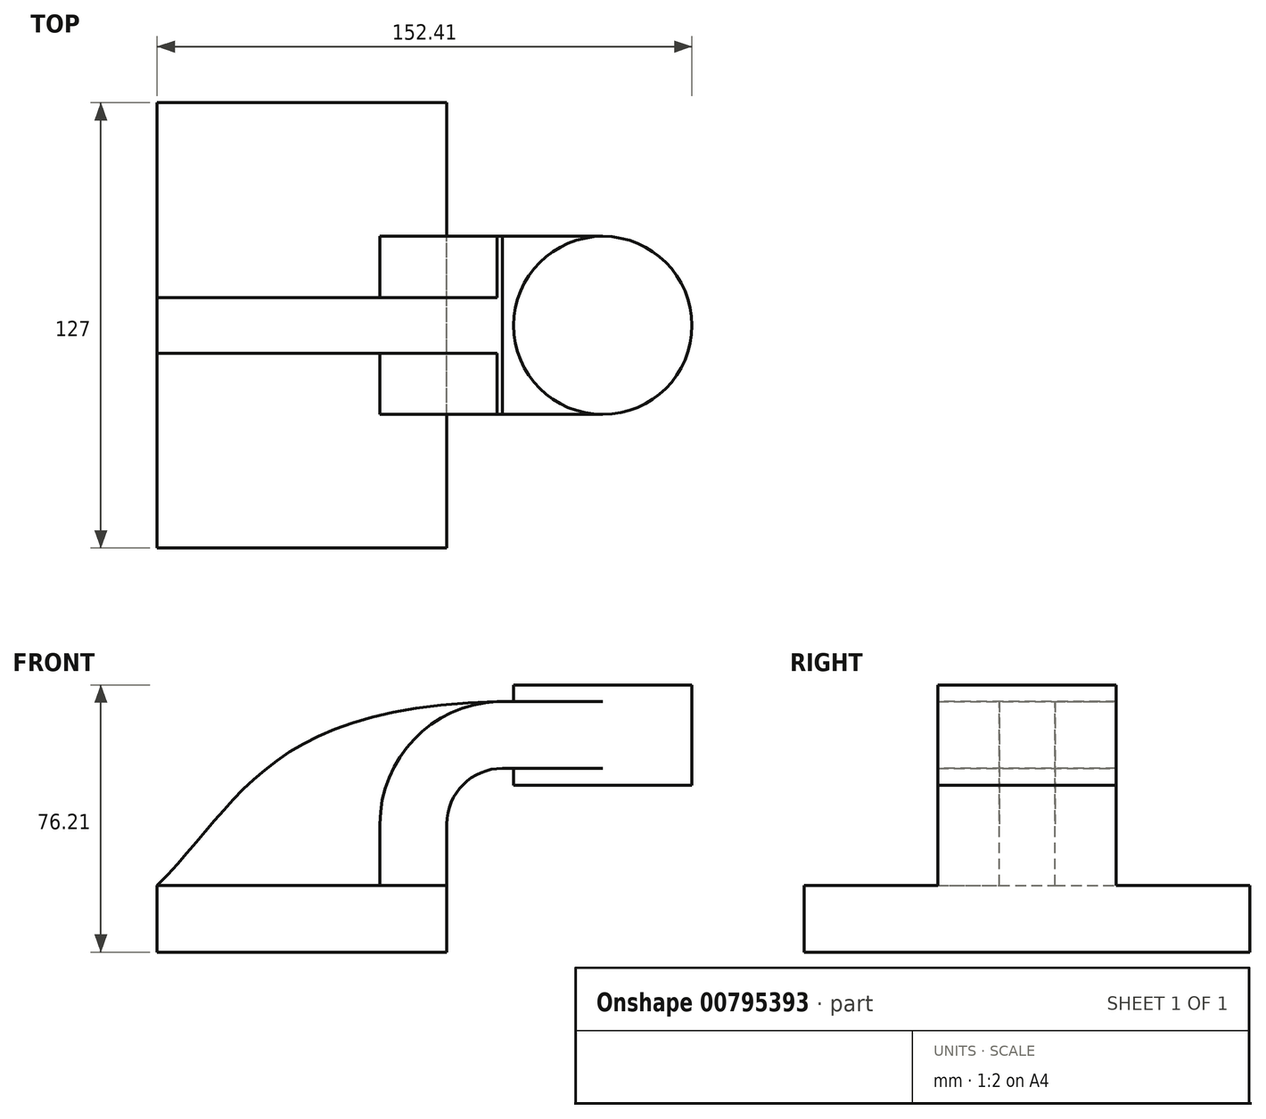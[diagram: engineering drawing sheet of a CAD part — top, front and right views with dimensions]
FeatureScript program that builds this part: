
annotation { "Feature Type Name" : "Feature", "Feature Type Description" : "" }
export const myFeature = defineFeature(function(context is Context, id is Id, definition is map)
    precondition{}
    {
        {
            var Q0;
            Q0=qCreatedBy(makeId("Front.planeOp"),FACE);
            var sketch = newSketch(context, id + "F0", { "sketchPlane" : qUnion([Q0])});
            skLineSegment(sketch, "E0.bottom", {"start": v(41.27, 9.53) * mm, "end": v(-41.28, 9.53) * mm});
            skLineSegment(sketch, "E0.top", {"start": v(41.28, -9.52) * mm, "end": v(-41.27, -9.52) * mm});
            skLineSegment(sketch, "E0.left", {"start": v(41.27, 9.53) * mm, "end": v(41.28, -9.52) * mm});
            skLineSegment(sketch, "E0.right", {"start": v(-41.28, 9.53) * mm, "end": v(-41.27, -9.52) * mm});
            skPoint(sketch, "E0.middle", {"position": v(0, 0) * mm});
            skLineSegment(sketch, "E1.bottom", {"start": v(111.12, 66.68) * mm, "end": v(60.32, 66.68) * mm});
            skLineSegment(sketch, "E1.top", {"start": v(111.12, 38.1) * mm, "end": v(60.32, 38.1) * mm});
            skLineSegment(sketch, "E1.left", {"start": v(111.12, 66.68) * mm, "end": v(111.12, 38.1) * mm});
            skLineSegment(sketch, "E1.right", {"start": v(60.32, 66.68) * mm, "end": v(60.32, 38.1) * mm});
            skPoint(sketch, "E1.middle", {"position": v(85.72, 52.39) * mm});
            skLineSegment(sketch, "E2", {"start": v(41.27, 9.53) * mm, "end": v(41.27, 27) * mm});
            skArc(sketch, "E3", {"start": v(41.27, 27) * mm, "mid": v(45.92, 38.23) * mm, "end": v(57.15, 42.88) * mm});
            skLineSegment(sketch, "E4", {"start": v(57.15, 42.88) * mm, "end": v(60.32, 42.88) * mm});
            skLineSegment(sketch, "E5.0", {"start": v(57.15, 61.93) * mm, "end": v(85.72, 61.93) * mm});
            skArc(sketch, "E5.1", {"start": v(22.22, 27) * mm, "mid": v(32.45, 51.7) * mm, "end": v(57.15, 61.93) * mm});
            skLineSegment(sketch, "E5.2", {"start": v(22.22, 9.53) * mm, "end": v(22.22, 27) * mm});
            skFitSpline(sketch, "E6", {"points": [v(-41.28, 9.53) * mm, v(57.15, 61.93) * mm], "startDerivative": vector(70.67, 69.68) * mm, "endDerivative": vector(203.24, 3.75) * mm});
            skLineSegment(sketch, "E7", {"start": v(85.72, 52.39) * mm, "end": v(85.72, 61.93) * mm});
            skLineSegment(sketch, "E8", {"start": v(60.32, 42.88) * mm, "end": v(85.72, 42.88) * mm});
            skLineSegment(sketch, "E9", {"start": v(85.72, 52.39) * mm, "end": v(85.72, 42.88) * mm});
            skLineSegment(sketch, "E10", {"start": v(85.72, 66.68) * mm, "end": v(85.72, 38.1) * mm});
            skSolve(sketch);
        }
        {
            var Q0;
            Q0=makeQuery(id+"F0.imprint","IMPRINT",FACE,{"disambiguationData":[TD([[makeQuery(id+"F0.imprint","IMPRINT",EDGE,{"derivedFrom":sQuery(id+"F0.wireOp",EDGE,"E0.top")}),-1.0]])]});
            extrude(context, id + "F1", {"entities" : qUnion([Q0]), "endBound" : BoundingType.SYMMETRIC, "depth" : 127 * mm, "offsetDistance" : 25.4 * mm});
        }
        {
            var Q0;
            {var subQ0=sQuery(id+"F0.wireOp",EDGE,"E2");Q0=makeQuery(id+"F0.imprint","IMPRINT",FACE,{"disambiguationData":[TD([[makeQuery(id+"F0.imprint","IMPRINT",EDGE,{"derivedFrom":subQ0}),1.0]])]});}
            var Q1;
            {var subQ1=sQuery(id+"F0.wireOp",EDGE,"E7");Q1=makeQuery(id+"F0.imprint","IMPRINT",FACE,{"disambiguationData":[TD([[makeQuery(id+"F0.imprint","IMPRINT",EDGE,{"derivedFrom":subQ1}),1.0]])]});}
            var Q2;
            {var subQ0=sQuery(id+"F0.wireOp",EDGE,"E8");Q2=makeQuery(id+"F0.imprint","IMPRINT",FACE,{"disambiguationData":[TD([[makeQuery(id+"F0.imprint","IMPRINT",EDGE,{"derivedFrom":subQ0}),1.0]])]});}
            extrude(context, id + "F2", {"entities" : qUnion([Q0, Q1, Q2]), "operationType" : NewBodyOperationType.ADD, "endBound" : BoundingType.SYMMETRIC, "depth" : 50.8 * mm, "offsetDistance" : 25.4 * mm});
        }
        {
            var Q0;
            {var subQ3=sQuery(id+"F0.wireOp",EDGE,"E5.2");Q0=makeQuery(id+"F0.imprint","IMPRINT",FACE,{"disambiguationData":[TD([[makeQuery(id+"F0.imprint","IMPRINT",EDGE,{"derivedFrom":subQ3}),1.0]])]});}
            extrude(context, id + "F3", {"entities" : qUnion([Q0]), "operationType" : NewBodyOperationType.ADD, "endBound" : BoundingType.SYMMETRIC, "depth" : 15.88 * mm, "offsetDistance" : 25.4 * mm});
        }
        {
            var Q0;
            {var subQ4=sQuery(id+"F0.wireOp",EDGE,"E1.left");Q0=makeQuery(id+"F0.imprint","IMPRINT",FACE,{"disambiguationData":[TD([[makeQuery(id+"F0.imprint","IMPRINT",EDGE,{"derivedFrom":subQ4}),-1.0]])]});}
            var Q1;
            Q1=sQuery(id+"F0.wireOp",EDGE,"E10");
            revolve(context, id + "F4", {"operationType" : NewBodyOperationType.ADD, "surfaceOperationType" : NewSurfaceOperationType.NEW, "entities" : qUnion([Q0]), "axis" : qUnion([Q1]), "revolveType" : RevolveType.FULL});
        }
    });
